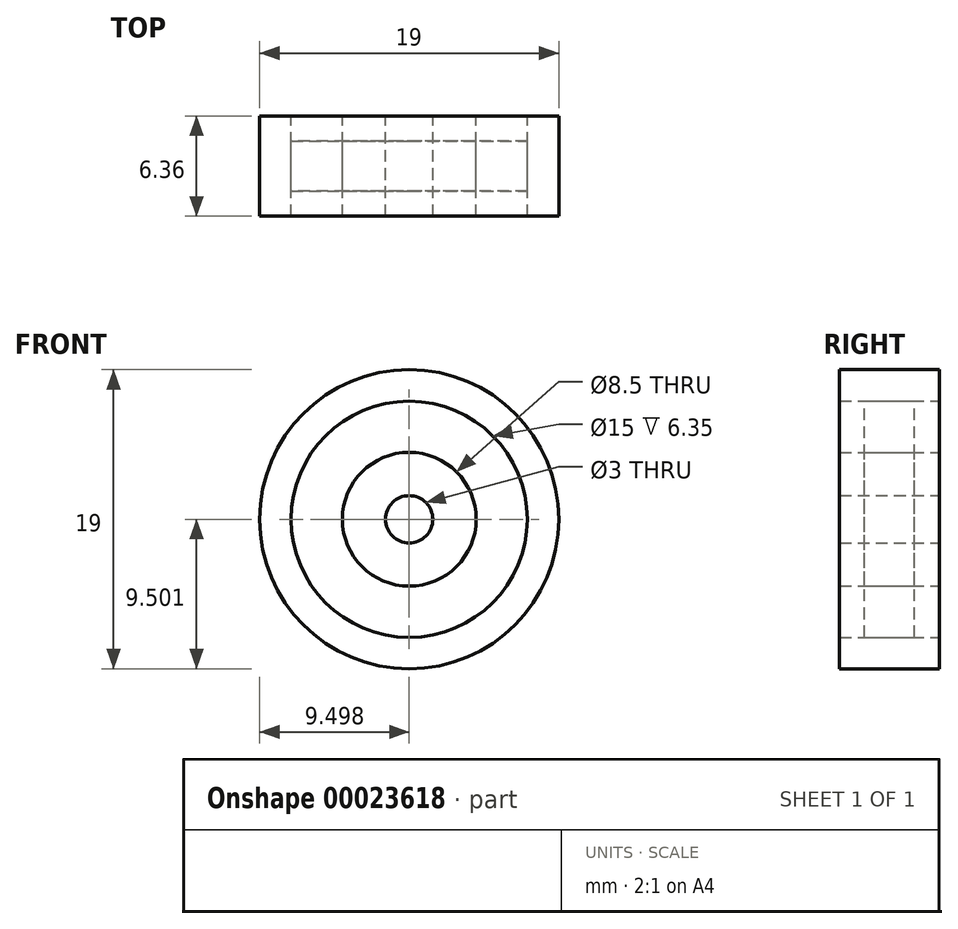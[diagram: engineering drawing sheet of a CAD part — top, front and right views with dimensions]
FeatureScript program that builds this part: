
annotation { "Feature Type Name" : "Feature", "Feature Type Description" : "" }
export const myFeature = defineFeature(function(context is Context, id is Id, definition is map)
    precondition{}
    {
        {
            var Q0;
            Q0=qCreatedBy(makeId("Front.planeOp"),FACE);
            var sketch = newSketch(context, id + "F0", { "sketchPlane" : qUnion([Q0])});
            skCircle(sketch, "E0", {"center": v(0.3, -0.15) * mm, "radius": 9.5 * mm});
            skCircle(sketch, "E1", {"center": v(0.3, -0.15) * mm, "radius": 7.5 * mm});
            skCircle(sketch, "E2", {"center": v(0.3, -0.15) * mm, "radius": 4.25 * mm});
            skCircle(sketch, "E3", {"center": v(0.3, -0.15) * mm, "radius": 1.5 * mm});
            skSolve(sketch);
        }
        {
            var Q0;
            Q0=makeQuery(id+"F0.imprint","IMPRINT",FACE,{"disambiguationData":[TD([[makeQuery(id+"F0.imprint","IMPRINT",EDGE,{"derivedFrom":sQuery(id+"F0.wireOp",EDGE,"E0")}),1.0]])]});
            var Q1;
            Q1=makeQuery(id+"F0.imprint","IMPRINT",FACE,{"disambiguationData":[TD([[makeQuery(id+"F0.imprint","IMPRINT",EDGE,{"derivedFrom":sQuery(id+"F0.wireOp",EDGE,"E2")}),1.0]])]});
            extrude(context, id + "F1", {"entities" : qUnion([Q0, Q1]), "endBound" : BoundingType.SYMMETRIC, "depth" : 6.35 * mm});
        }
        {
            var Q0;
            Q0=makeQuery(id+"F0.imprint","IMPRINT",FACE,{"disambiguationData":[TD([[makeQuery(id+"F0.imprint","IMPRINT",EDGE,{"derivedFrom":sQuery(id+"F0.wireOp",EDGE,"E1")}),1.0]])]});
            extrude(context, id + "F2", {"entities" : qUnion([Q0]), "endBound" : BoundingType.SYMMETRIC, "depth" : 3.17 * mm});
        }
    });
